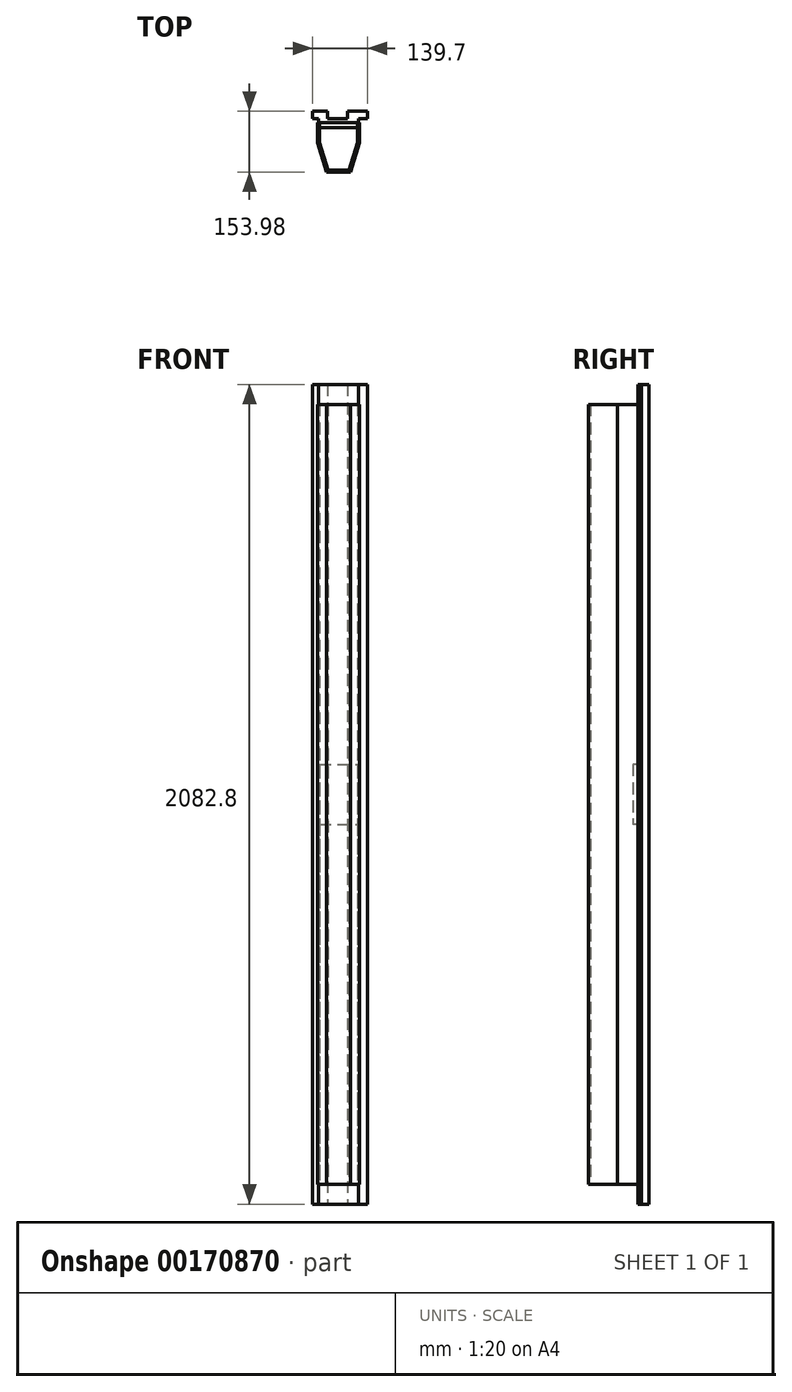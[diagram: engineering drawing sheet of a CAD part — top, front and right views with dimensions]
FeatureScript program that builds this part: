
annotation { "Feature Type Name" : "Feature", "Feature Type Description" : "" }
export const myFeature = defineFeature(function(context is Context, id is Id, definition is map)
    precondition{}
    {
        {
            var Q0;
            Q0=qCreatedBy(makeId("Top.planeOp"),FACE);
            var sketch = newSketch(context, id + "F0", { "sketchPlane" : qUnion([Q0])});
            skLineSegment(sketch, "E0", {"start": v(-48.42, 0) * mm, "end": v(-48.42, -50.8) * mm});
            skLineSegment(sketch, "E1", {"start": v(-48.42, -50.8) * mm, "end": v(-26.99, -120.65) * mm});
            skLineSegment(sketch, "E2", {"start": v(-26.99, -120.65) * mm, "end": v(26.99, -120.65) * mm});
            skLineSegment(sketch, "E3", {"start": v(26.99, -120.65) * mm, "end": v(48.42, -50.8) * mm});
            skLineSegment(sketch, "E4", {"start": v(48.42, -50.8) * mm, "end": v(48.42, 0) * mm});
            skLineSegment(sketch, "E5.0", {"start": v(53.18, -51.51) * mm, "end": v(53.18, 0) * mm});
            skLineSegment(sketch, "E5.1", {"start": v(-53.18, 0) * mm, "end": v(-53.18, -51.51) * mm});
            skLineSegment(sketch, "E5.2", {"start": v(-53.18, -51.51) * mm, "end": v(-30.5, -125.41) * mm});
            skLineSegment(sketch, "E5.3", {"start": v(-30.5, -125.41) * mm, "end": v(30.5, -125.41) * mm});
            skLineSegment(sketch, "E5.4", {"start": v(30.5, -125.41) * mm, "end": v(53.18, -51.51) * mm});
            skLineSegment(sketch, "E6", {"start": v(-53.18, 0) * mm, "end": v(-48.42, 0) * mm});
            skLineSegment(sketch, "E7", {"start": v(48.42, 0) * mm, "end": v(53.18, 0) * mm});
            skSolve(sketch);
        }
        {
            var Q0;
            Q0 = qSketchRegion(id + "F0", true);
            extrude(context, id + "F1", {"entities" : qUnion([Q0]), "depth" : 1981.2 * mm});
        }
        {
            var Q0;
            Q0=qCreatedBy(makeId("Top.planeOp"),FACE);
            cPlane(context, id + "F2", {"entities" : qUnion([Q0]), "cplaneType" : CPlaneType.OFFSET, "offset" : 990.6 * mm, "width" : 152.4 * mm, "height" : 152.4 * mm});
        }
        {
            var Q0;
            Q0=qCreatedBy(id+"F2.planeOp",FACE);
            var sketch = newSketch(context, id + "F3", { "sketchPlane" : qUnion([Q0])});
            skLineSegment(sketch, "E8.bottom", {"start": v(-48.42, 0) * mm, "end": v(48.42, 0) * mm});
            skLineSegment(sketch, "E8.top", {"start": v(-48.42, -12.7) * mm, "end": v(48.42, -12.7) * mm});
            skLineSegment(sketch, "E8.left", {"start": v(-48.42, 0) * mm, "end": v(-48.42, -12.7) * mm});
            skLineSegment(sketch, "E8.right", {"start": v(48.42, 0) * mm, "end": v(48.42, -12.7) * mm});
            skSolve(sketch);
        }
        {
            var Q0;
            Q0 = qSketchRegion(id + "F3", true);
            extrude(context, id + "F4", {"entities" : qUnion([Q0]), "operationType" : NewBodyOperationType.ADD, "depth" : 76.2 * mm, "hasSecondDirection" : true, "secondDirectionOppositeDirection" : true, "secondDirectionDepth" : 76.2 * mm});
        }
        {
            var Q0;
            Q0=qCreatedBy(id+"F2.planeOp",FACE);
            var sketch = newSketch(context, id + "F5", { "sketchPlane" : qUnion([Q0])});
            skLineSegment(sketch, "E9.bottom", {"start": v(-50.8, 0) * mm, "end": v(50.8, 0) * mm});
            skLineSegment(sketch, "E9.top", {"start": v(-50.8, 9.52) * mm, "end": v(50.8, 9.52) * mm});
            skLineSegment(sketch, "E9.left", {"start": v(-50.8, 0) * mm, "end": v(-50.8, 9.52) * mm});
            skLineSegment(sketch, "E9.right", {"start": v(50.8, 0) * mm, "end": v(50.8, 9.53) * mm});
            skSolve(sketch);
        }
        {
            var Q0;
            Q0 = qSketchRegion(id + "F5", true);
            extrude(context, id + "F6", {"entities" : qUnion([Q0]), "operationType" : NewBodyOperationType.ADD, "depth" : 1041.4 * mm, "hasSecondDirection" : true, "secondDirectionOppositeDirection" : true, "secondDirectionDepth" : 1041.4 * mm});
        }
        {
            var Q0;
            Q0=qCreatedBy(id+"F2.planeOp",FACE);
            var sketch = newSketch(context, id + "F7", { "sketchPlane" : qUnion([Q0])});
            skLineSegment(sketch, "E10.bottom", {"start": v(23.02, 9.52) * mm, "end": v(73.82, 9.52) * mm});
            skLineSegment(sketch, "E10.top", {"start": v(23.02, 28.57) * mm, "end": v(73.82, 28.57) * mm});
            skLineSegment(sketch, "E10.left", {"start": v(23.02, 9.52) * mm, "end": v(23.02, 28.57) * mm});
            skLineSegment(sketch, "E10.right", {"start": v(73.82, 9.52) * mm, "end": v(73.82, 28.57) * mm});
            skLineSegment(sketch, "E11.bottom", {"start": v(-65.88, 9.52) * mm, "end": v(-27.78, 9.52) * mm});
            skLineSegment(sketch, "E11.top", {"start": v(-65.88, 28.57) * mm, "end": v(-27.78, 28.57) * mm});
            skLineSegment(sketch, "E11.left", {"start": v(-65.88, 9.52) * mm, "end": v(-65.88, 28.57) * mm});
            skLineSegment(sketch, "E11.right", {"start": v(-27.78, 9.52) * mm, "end": v(-27.78, 28.57) * mm});
            skSolve(sketch);
        }
        {
            var Q0;
            Q0=makeQuery(id+"F7.imprint","IMPRINT",FACE,{"disambiguationData":[TD([[makeQuery(id+"F7.imprint","IMPRINT",EDGE,{"derivedFrom":sQuery(id+"F7.wireOp",EDGE,"E10.bottom")}),1.0]])]});
            var Q1;
            Q1=makeQuery(id+"F7.imprint","IMPRINT",FACE,{"disambiguationData":[TD([[makeQuery(id+"F7.imprint","IMPRINT",EDGE,{"derivedFrom":sQuery(id+"F7.wireOp",EDGE,"E11.bottom")}),1.0]])]});
            extrude(context, id + "F8", {"entities" : qUnion([Q0, Q1]), "operationType" : NewBodyOperationType.ADD, "depth" : 1041.4 * mm, "hasSecondDirection" : true, "secondDirectionOppositeDirection" : true, "secondDirectionDepth" : 1041.4 * mm});
        }
    });
